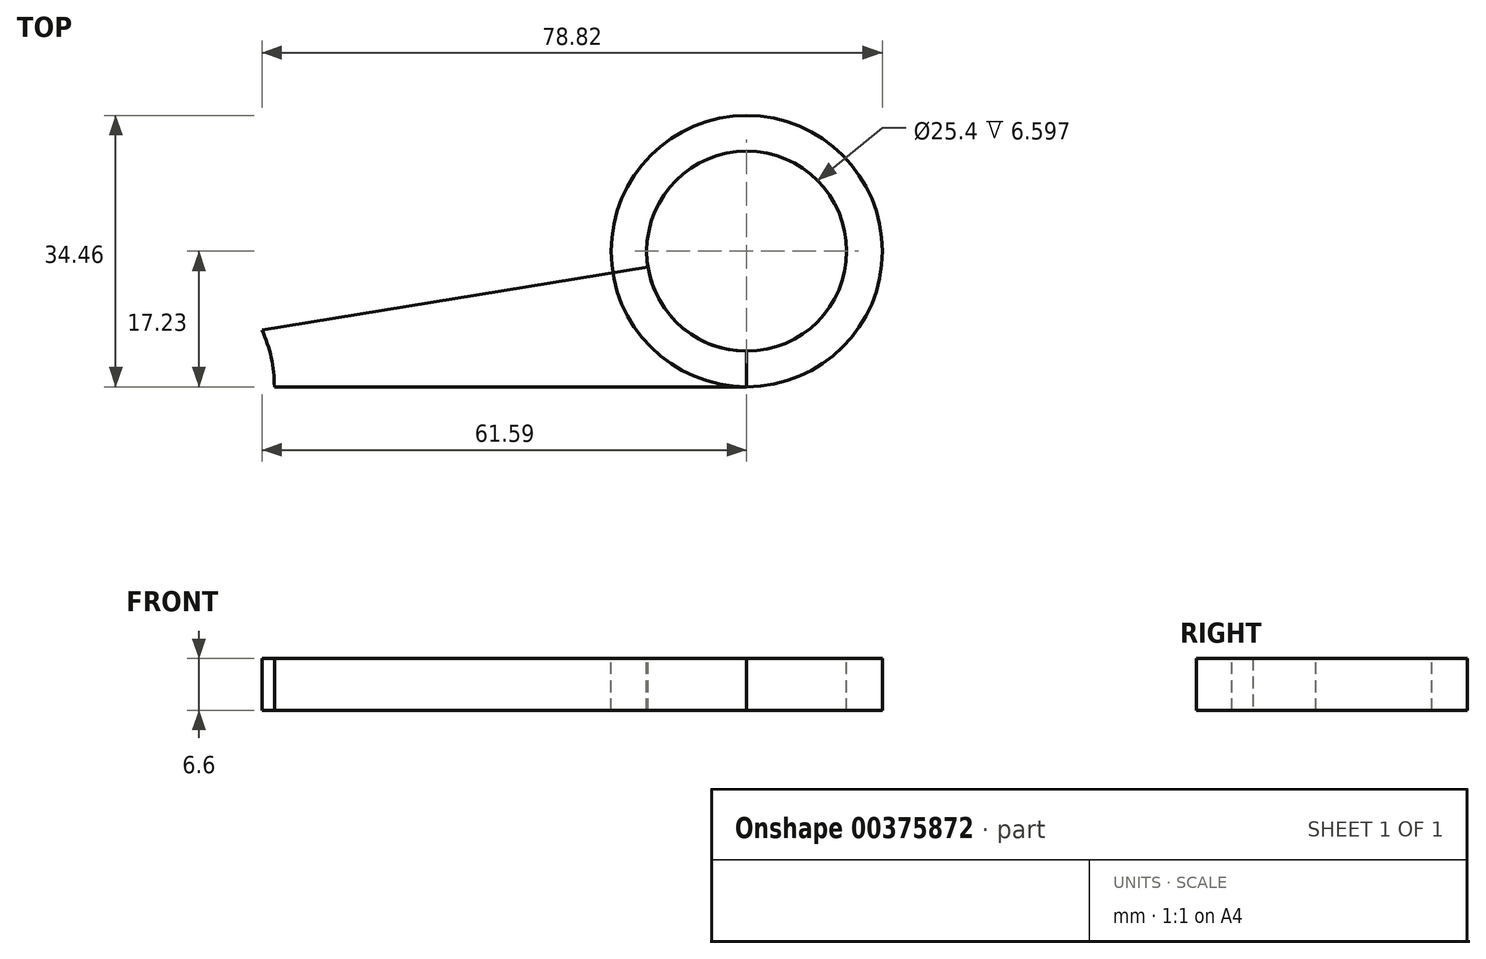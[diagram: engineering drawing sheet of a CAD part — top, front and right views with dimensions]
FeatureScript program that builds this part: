
annotation { "Feature Type Name" : "Feature", "Feature Type Description" : "" }
export const myFeature = defineFeature(function(context is Context, id is Id, definition is map)
    precondition{}
    {
        {
            var Q0;
            Q0=qCreatedBy(makeId("Top.planeOp"),FACE);
            var sketch = newSketch(context, id + "F0", { "sketchPlane" : qUnion([Q0])});
            skLineSegment(sketch, "E0.bottom", {"start": v(0, 0) * mm, "end": v(-77.23, 0) * mm});
            skLineSegment(sketch, "E0.top", {"start": v(0, -17.23) * mm, "end": v(-77.23, -17.23) * mm});
            skLineSegment(sketch, "E0.left", {"start": v(0, 0) * mm, "end": v(0, -17.23) * mm});
            skLineSegment(sketch, "E0.right", {"start": v(-77.23, 0) * mm, "end": v(-77.23, -17.23) * mm});
            skSolve(sketch);
        }
        {
            var Q0;
            Q0=makeQuery(id+"F0.imprint","IMPRINT",FACE,{"disambiguationData":[TD([[makeQuery(id+"F0.imprint","IMPRINT",EDGE,{"derivedFrom":sQuery(id+"F0.wireOp",EDGE,"E0.bottom")}),1.0]])]});
            extrude(context, id + "F1", {"entities" : qUnion([Q0]), "depth" : 6.6 * mm});
        }
        {
            var Q0;
            Q0=makeQuery(id+"F1.opExtrude","SWEPT_FACE",FACE,{"disambiguationData":[OSD([sQuery(id+"F0.wireOp",EDGE,"E0.bottom")])]});
            var Q1;
            Q1=makeQuery(id+"F1.opExtrude","SWEPT_EDGE",EDGE,{"disambiguationData":[OSD([sQuery(id+"F0.wireOp",EDGE,"E0.bottom"),sQuery(id+"F0.wireOp",EDGE,"E0.left")])]});
            revolve(context, id + "F2", {"operationType" : NewBodyOperationType.REMOVE, "entities" : qUnion([Q0]), "axis" : qUnion([Q1]), "revolveType" : RevolveType.SYMMETRIC, "angle" : 18.44 * degree});
        }
        {
            var Q0;
            Q0=makeQuery(id+"F1.opExtrude","SWEPT_FACE",FACE,{"disambiguationData":[OSD([sQuery(id+"F0.wireOp",EDGE,"E0.left")])]});
            var Q1;
            {var subQ0=sQuery(id+"F0.wireOp",EDGE,"E0.left");var subQ1=sQuery(id+"F0.wireOp",EDGE,"E0.bottom");Q1=makeQuery(id+"F2.boolean.opBoolean","MERGE",EDGE,{"derivedFrom":[makeQuery(id+"F1.opExtrude","SWEPT_EDGE",EDGE,{"disambiguationData":[OSD([subQ1,subQ0])]}),makeQuery(id+"F2.opRevolve","CAP_EDGE",EDGE,{"disambiguationData":[OSD([subQ1,subQ0])],"isStart":true})]});}
            revolve(context, id + "F3", {"entities" : qUnion([Q0]), "axis" : qUnion([Q1]), "revolveType" : RevolveType.FULL});
        }
        {
            var Q0;
            {var subQ0=sQuery(id+"F0.wireOp",EDGE,"E0.left");Q0=makeQuery(id+"F3.opRevolve","SWEPT_FACE",FACE,{"disambiguationData":[OSD([subQ0]),TDD([makeQuery(id+"F1.opExtrude","CAP_EDGE",EDGE,{"disambiguationData":[OSD([subQ0])],"isStart":false})])]});}
            var sketch = newSketch(context, id + "F4", { "sketchPlane" : qUnion([Q0])});
            skPoint(sketch, "E1", {"position": v(0, 0) * mm});
            skPoint(sketch, "E2", {"position": v(26.8, 10.97) * mm});
            skSolve(sketch);
        }
        {
            var Q0;
            Q0=sQuery(id+"F4.wireOp",VERTEX,"E1");
            var Q1;
            Q1=makeQuery(id+"F1.opExtrude","SWEPT_BODY",BODY,{"disambiguationData":[OSD([sQuery(id+"F0.wireOp",EDGE,"E0.bottom"),sQuery(id+"F0.wireOp",EDGE,"E0.top"),sQuery(id+"F0.wireOp",EDGE,"E0.left"),sQuery(id+"F0.wireOp",EDGE,"E0.right")])]});
            var Q2;
            Q2=makeQuery(id+"F3.opRevolve","SWEPT_BODY",BODY,{"disambiguationData":[OSD([sQuery(id+"F0.wireOp",EDGE,"E0.left")])]});
            hole(context, id + "F5", {"style" : HoleStyle.SIMPLE, "endStyle" : HoleEndStyle.THROUGH, "holeDiameter" : 25.4 * mm, "isTappedThrough" : true, "tappedDepth" : 12.7 * mm, "tapClearance" : 3, "locations" : qUnion([Q0]), "scope" : qUnion([Q1, Q2])});
        }
        {
            var Q0;
            Q0=makeQuery(id+"F1.opExtrude","SWEPT_FACE",FACE,{"disambiguationData":[OSD([sQuery(id+"F0.wireOp",EDGE,"E0.right")])]});
            var Q1;
            Q1=makeQuery(id+"F1.opExtrude","SWEPT_EDGE",EDGE,{"disambiguationData":[OSD([sQuery(id+"F0.wireOp",EDGE,"E0.top"),sQuery(id+"F0.wireOp",EDGE,"E0.right")])]});
            revolve(context, id + "F6", {"operationType" : NewBodyOperationType.REMOVE, "entities" : qUnion([Q0]), "axis" : qUnion([Q1]), "revolveType" : RevolveType.FULL, "oppositeDirection" : true});
        }
        {
            var Q0;
            Q0=makeQuery(id+"F1.opExtrude","SWEPT_FACE",FACE,{"disambiguationData":[OSD([sQuery(id+"F0.wireOp",EDGE,"E0.top")])]});
            var Q1;
            Q1=makeQuery(id+"F6.boolean.opBoolean","INTERSECT",EDGE,{"derivedFrom":[makeQuery(id+"F1.opExtrude","SWEPT_FACE",FACE,{"disambiguationData":[OSD([sQuery(id+"F0.wireOp",EDGE,"E0.top")])]}),makeQuery(id+"F6.opRevolve","SWEPT_FACE",FACE,{"disambiguationData":[OSD([sQuery(id+"F0.wireOp",EDGE,"E0.bottom"),sQuery(id+"F0.wireOp",EDGE,"E0.right")])]})]});
            var Q2;
            {var subQ0=sQuery(id+"F0.wireOp",EDGE,"E0.bottom");Q2=makeQuery(id+"F6.boolean.opBoolean","INTERSECT",EDGE,{"derivedFrom":[makeQuery(id+"F2.boolean.opBoolean","COPY",FACE,{"derivedFrom":makeQuery(id+"F2.opRevolve","CAP_FACE",FACE,{"disambiguationData":[OSD([subQ0])],"isStart":true})}),makeQuery(id+"F6.opRevolve","SWEPT_FACE",FACE,{"disambiguationData":[OSD([subQ0,sQuery(id+"F0.wireOp",EDGE,"E0.right")])]})]});}
            revolve(context, id + "F7", {"bodyType" : ToolBodyType.SURFACE, "entities" : qUnion([Q0]), "surfaceEntities" : qUnion([Q1]), "axis" : qUnion([Q2]), "revolveType" : RevolveType.FULL});
        }
    });
